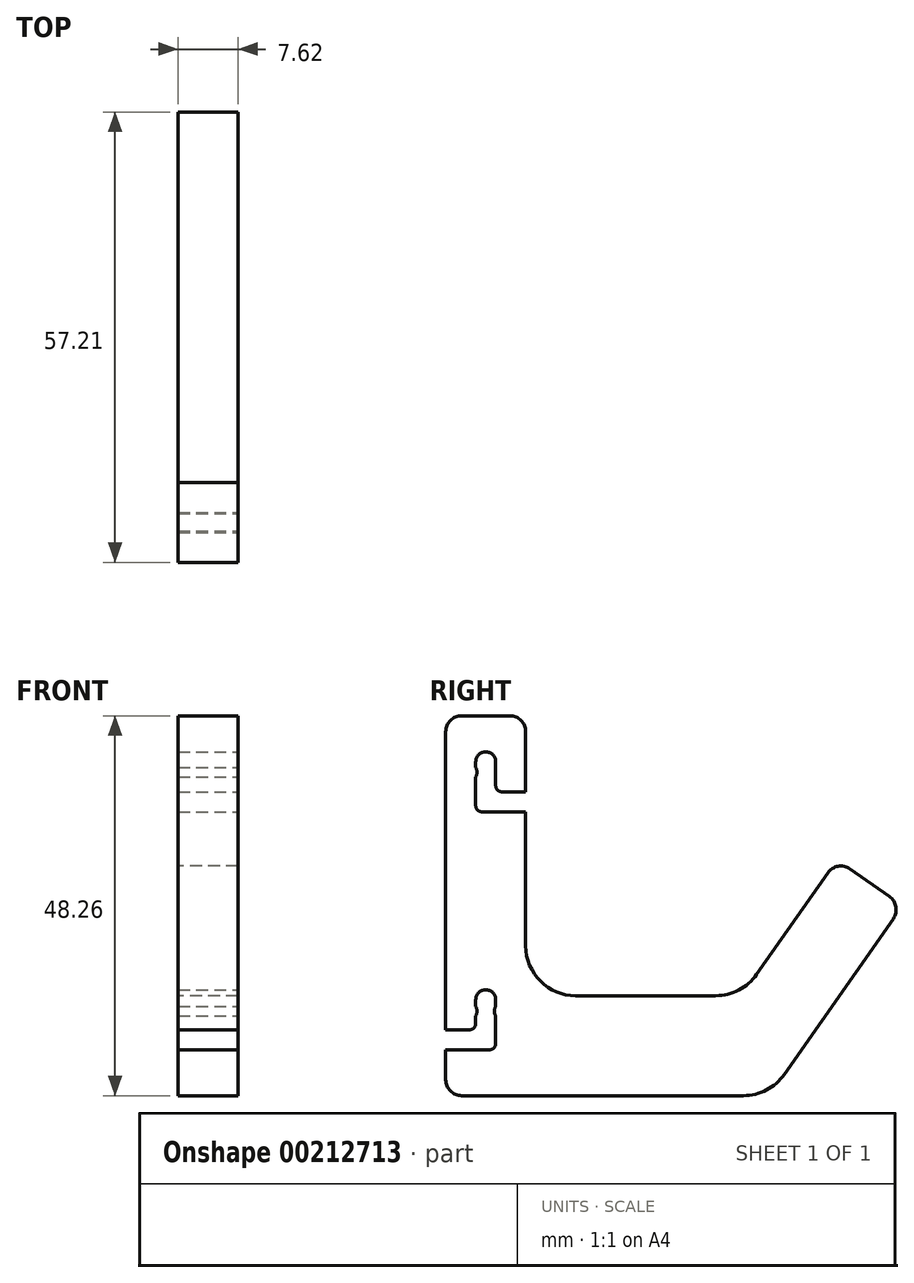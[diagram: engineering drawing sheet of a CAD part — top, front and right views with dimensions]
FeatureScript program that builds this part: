
annotation { "Feature Type Name" : "Feature", "Feature Type Description" : "" }
export const myFeature = defineFeature(function(context is Context, id is Id, definition is map)
    precondition{}
    {
        {
            var Q0;
            Q0=qCreatedBy(makeId("Right.planeOp"),FACE);
            var sketch = newSketch(context, id + "F0", { "sketchPlane" : qUnion([Q0])});
            skLineSegment(sketch, "E0", {"start": v(0, 0) * mm, "end": v(0, 43.18) * mm});
            skLineSegment(sketch, "E1", {"start": v(0, 43.18) * mm, "end": v(10.16, 43.18) * mm});
            skLineSegment(sketch, "E2", {"start": v(10.16, 43.18) * mm, "end": v(10.16, 13.97) * mm});
            skLineSegment(sketch, "E3", {"start": v(0, 0) * mm, "end": v(0, 0) * mm});
            skLineSegment(sketch, "E4", {"start": v(16.51, 7.62) * mm, "end": v(34.3, 7.62) * mm});
            skLineSegment(sketch, "E5", {"start": v(39.5, 10.33) * mm, "end": v(49.69, 24.9) * mm});
            skLineSegment(sketch, "E6", {"start": v(49.69, 24.9) * mm, "end": v(58.01, 19.06) * mm});
            skLineSegment(sketch, "E7", {"start": v(58.01, 19.06) * mm, "end": v(43, -2.37) * mm});
            skArc(sketch, "E8", {"start": v(34.3, 7.62) * mm, "mid": v(37.22, 8.34) * mm, "end": v(39.5, 10.33) * mm});
            skArc(sketch, "E9", {"start": v(10.16, 13.97) * mm, "mid": v(12.02, 9.48) * mm, "end": v(16.51, 7.62) * mm});
            skArc(sketch, "E10.filletArc", {"start": v(37.8, -5.08) * mm, "mid": v(40.73, -4.36) * mm, "end": v(43, -2.37) * mm});
            skLineSegment(sketch, "E11", {"start": v(0, 0) * mm, "end": v(0, -5.08) * mm});
            skLineSegment(sketch, "E12", {"start": v(0, -5.08) * mm, "end": v(37.8, -5.08) * mm});
            skSolve(sketch);
        }
        {
            var Q0;
            Q0=makeQuery(id+"F0.imprint","IMPRINT",FACE,{"disambiguationData":[TD([[makeQuery(id+"F0.imprint","IMPRINT",EDGE,{"derivedFrom":sQuery(id+"F0.wireOp",EDGE,"E0")}),-1.0]])]});
            extrude(context, id + "F1", {"entities" : qUnion([Q0]), "depth" : 7.62 * mm, "symmetric" : true});
        }
        {
            var Q0;
            Q0=makeQuery(id+"F1.opExtrude","SWEPT_EDGE",EDGE,{"disambiguationData":[OSD([sQuery(id+"F0.wireOp",EDGE,"E1"),sQuery(id+"F0.wireOp",EDGE,"E2")])]});
            var Q1;
            Q1=makeQuery(id+"F1.opExtrude","SWEPT_EDGE",EDGE,{"disambiguationData":[OSD([sQuery(id+"F0.wireOp",EDGE,"do6iOSd0-p59h-Iph2-EZYE-FqhHj6ALnol1"),sQuery(id+"F0.wireOp",EDGE,"T0NzOJQf-1ohU-N6pa-0O5Z-Gt8aX7xeZM4e")])]});
            var Q2;
            Q2=makeQuery(id+"F1.opExtrude","SWEPT_EDGE",EDGE,{"disambiguationData":[OSD([sQuery(id+"F0.wireOp",EDGE,"do6iOSd0-p59h-Iph2-EZYE-FqhHj6ALnol1"),sQuery(id+"F0.wireOp",EDGE,"WKioYHe8-msfK-nLwt-kgpN-sC7kTCiPyutY")])]});
            var Q3;
            Q3=makeQuery(id+"F1.opExtrude","SWEPT_EDGE",EDGE,{"disambiguationData":[OSD([sQuery(id+"F0.wireOp",EDGE,"do6iOSd0-p59h-Iph2-EZYE-FqhHj6ALnol1"),sQuery(id+"F0.wireOp",EDGE,"T0NzOJQf-1ohU-N6pa-0O5Z-Gt8aX7xeZM4e")])]});
            var Q4;
            Q4=makeQuery(id+"F1.opExtrude","SWEPT_EDGE",EDGE,{"disambiguationData":[OSD([sQuery(id+"F0.wireOp",EDGE,"do6iOSd0-p59h-Iph2-EZYE-FqhHj6ALnol1"),sQuery(id+"F0.wireOp",EDGE,"WKioYHe8-msfK-nLwt-kgpN-sC7kTCiPyutY")])]});
            var Q5;
            Q5=makeQuery(id+"F1.opExtrude","SWEPT_EDGE",EDGE,{"disambiguationData":[OSD([sQuery(id+"F0.wireOp",EDGE,"E1"),sQuery(id+"F0.wireOp",EDGE,"917d6a71-8020-47b3-91d0-356564592358.trimOffspring")])]});
            var Q6;
            Q6=makeQuery(id+"F1.opExtrude","SWEPT_EDGE",EDGE,{"disambiguationData":[OSD([sQuery(id+"F0.wireOp",EDGE,"E1"),sQuery(id+"F0.wireOp",EDGE,"E2")])]});
            var Q7;
            Q7=makeQuery(id+"F1.opExtrude","SWEPT_EDGE",EDGE,{"disambiguationData":[OSD([sQuery(id+"F0.wireOp",EDGE,"E1"),sQuery(id+"F0.wireOp",EDGE,"917d6a71-8020-47b3-91d0-356564592358.trimOffspring")])]});
            var Q8;
            Q8=makeQuery(id+"F1.opExtrude","SWEPT_EDGE",EDGE,{"disambiguationData":[OSD([sQuery(id+"F0.wireOp",EDGE,"E1"),sQuery(id+"F0.wireOp",EDGE,"917d6a71-8020-47b3-91d0-356564592358.trimOffspring")])]});
            var Q9;
            Q9=makeQuery(id+"F1.opExtrude","SWEPT_EDGE",EDGE,{"disambiguationData":[OSD([sQuery(id+"F0.wireOp",EDGE,"917d6a71-8020-47b3-91d0-356564592358.trimOffspring"),sQuery(id+"F0.wireOp",EDGE,"oMnLxIvI-c7EB-dOBx-Ktot-nHqWXF2Je9gS")])]});
            var Q10;
            Q10=makeQuery(id+"F1.opExtrude","SWEPT_EDGE",EDGE,{"disambiguationData":[OSD([sQuery(id+"F0.wireOp",EDGE,"E0"),sQuery(id+"F0.wireOp",EDGE,"H5s6PmsO-nB2p-iTXC-beMi-EFhrGGPzX9zd")])]});
            var Q11;
            Q11=makeQuery(id+"F1.opExtrude","SWEPT_EDGE",EDGE,{"disambiguationData":[OSD([sQuery(id+"F0.wireOp",EDGE,"E0"),sQuery(id+"F0.wireOp",EDGE,"H5s6PmsO-nB2p-iTXC-beMi-EFhrGGPzX9zd")])]});
            var Q12;
            Q12=makeQuery(id+"F1.opExtrude","SWEPT_EDGE",EDGE,{"disambiguationData":[OSD([sQuery(id+"F0.wireOp",EDGE,"E0"),sQuery(id+"F0.wireOp",EDGE,"H5s6PmsO-nB2p-iTXC-beMi-EFhrGGPzX9zd")])]});
            var Q13;
            Q13=makeQuery(id+"F1.opExtrude","SWEPT_EDGE",EDGE,{"disambiguationData":[OSD([sQuery(id+"F0.wireOp",EDGE,"E0"),sQuery(id+"F0.wireOp",EDGE,"H5s6PmsO-nB2p-iTXC-beMi-EFhrGGPzX9zd")])]});
            var Q14;
            Q14=makeQuery(id+"F1.opExtrude","SWEPT_EDGE",EDGE,{"disambiguationData":[OSD([sQuery(id+"F0.wireOp",EDGE,"tsVY66jG-GQxW-Nj7m-msUx-ij5FFVlZpnMZ"),sQuery(id+"F0.wireOp",EDGE,"p4fpiYAK-jGJt-w9eP-5vz1-EoqmOrb9To5q")])]});
            var Q15;
            Q15=makeQuery(id+"F1.opExtrude","SWEPT_EDGE",EDGE,{"disambiguationData":[OSD([sQuery(id+"F0.wireOp",EDGE,"tsVY66jG-GQxW-Nj7m-msUx-ij5FFVlZpnMZ"),sQuery(id+"F0.wireOp",EDGE,"pGC2duow-bWWV-YhgJ-DpL9-4p7fWgwL10ZT")])]});
            var Q16;
            Q16=makeQuery(id+"F1.opExtrude","SWEPT_EDGE",EDGE,{"disambiguationData":[OSD([sQuery(id+"F0.wireOp",EDGE,"tsVY66jG-GQxW-Nj7m-msUx-ij5FFVlZpnMZ"),sQuery(id+"F0.wireOp",EDGE,"pGC2duow-bWWV-YhgJ-DpL9-4p7fWgwL10ZT")])]});
            var Q17;
            Q17=makeQuery(id+"F1.opExtrude","SWEPT_EDGE",EDGE,{"disambiguationData":[OSD([sQuery(id+"F0.wireOp",EDGE,"tsVY66jG-GQxW-Nj7m-msUx-ij5FFVlZpnMZ"),sQuery(id+"F0.wireOp",EDGE,"p4fpiYAK-jGJt-w9eP-5vz1-EoqmOrb9To5q")])]});
            var Q18;
            Q18=makeQuery(id+"F1.opExtrude","SWEPT_EDGE",EDGE,{"disambiguationData":[OSD([sQuery(id+"F0.wireOp",EDGE,"tsVY66jG-GQxW-Nj7m-msUx-ij5FFVlZpnMZ"),sQuery(id+"F0.wireOp",EDGE,"pGC2duow-bWWV-YhgJ-DpL9-4p7fWgwL10ZT")])]});
            var Q19;
            Q19=makeQuery(id+"F1.opExtrude","SWEPT_EDGE",EDGE,{"disambiguationData":[OSD([sQuery(id+"F0.wireOp",EDGE,"l7jfHRW3-1uXe-nOm0-suk0-xWNmDAWcYurH"),sQuery(id+"F0.wireOp",EDGE,"E3")])]});
            var Q20;
            Q20=makeQuery(id+"F1.opExtrude","SWEPT_EDGE",EDGE,{"disambiguationData":[OSD([sQuery(id+"F0.wireOp",EDGE,"E5"),sQuery(id+"F0.wireOp",EDGE,"E6")])]});
            var Q21;
            Q21=makeQuery(id+"F1.opExtrude","SWEPT_EDGE",EDGE,{"disambiguationData":[OSD([sQuery(id+"F0.wireOp",EDGE,"E6"),sQuery(id+"F0.wireOp",EDGE,"E7")])]});
            var Q22;
            Q22=makeQuery(id+"F1.opExtrude","SWEPT_EDGE",EDGE,{"disambiguationData":[OSD([sQuery(id+"F0.wireOp",EDGE,"E11"),sQuery(id+"F0.wireOp",EDGE,"E12")])]});
            fillet(context, id + "F2", {"entities" : qUnion([Q0, Q1, Q2, Q3, Q4, Q5, Q6, Q7, Q8, Q9, Q10, Q11, Q12, Q13, Q14, Q15, Q16, Q17, Q18, Q19, Q20, Q21, Q22]), "radius" : 2.03 * mm, "tangentPropagation" : true, "allowEdgeOverflow" : false});
        }
        {
            var Q0;
            Q0=makeQuery(id+"F1.opExtrude","CAP_FACE",FACE,{"disambiguationData":[OSD([sQuery(id+"F0.wireOp",EDGE,"E0"),sQuery(id+"F0.wireOp",EDGE,"E1"),sQuery(id+"F0.wireOp",EDGE,"917d6a71-8020-47b3-91d0-356564592358.trimOffspring"),sQuery(id+"F0.wireOp",EDGE,"do6iOSd0-p59h-Iph2-EZYE-FqhHj6ALnol1"),sQuery(id+"F0.wireOp",EDGE,"E2"),sQuery(id+"F0.wireOp",EDGE,"oMnLxIvI-c7EB-dOBx-Ktot-nHqWXF2Je9gS"),sQuery(id+"F0.wireOp",EDGE,"H5s6PmsO-nB2p-iTXC-beMi-EFhrGGPzX9zd"),sQuery(id+"F0.wireOp",EDGE,"E55nDa4c-AnYE-asiw-xueP-FGOoVfwC6I5W"),sQuery(id+"F0.wireOp",EDGE,"tsVY66jG-GQxW-Nj7m-msUx-ij5FFVlZpnMZ"),sQuery(id+"F0.wireOp",EDGE,"WKioYHe8-msfK-nLwt-kgpN-sC7kTCiPyutY"),sQuery(id+"F0.wireOp",EDGE,"pGC2duow-bWWV-YhgJ-DpL9-4p7fWgwL10ZT"),sQuery(id+"F0.wireOp",EDGE,"l7jfHRW3-1uXe-nOm0-suk0-xWNmDAWcYurH"),sQuery(id+"F0.wireOp",EDGE,"p4fpiYAK-jGJt-w9eP-5vz1-EoqmOrb9To5q"),sQuery(id+"F0.wireOp",EDGE,"E3"),sQuery(id+"F0.wireOp",EDGE,"yA7TRvCN-UMRo-vrpZ-Ydxq-uWrTOSylFOQI"),sQuery(id+"F0.wireOp",EDGE,"T0NzOJQf-1ohU-N6pa-0O5Z-Gt8aX7xeZM4e"),sQuery(id+"F0.wireOp",EDGE,"pUJUahGI-wT5O-X5Pp-sLFv-ISeCsSa39cJM"),sQuery(id+"F0.wireOp",EDGE,"gnTElwEQ-xExs-yJdp-y54U-xUUldCR7EacK"),sQuery(id+"F0.wireOp",EDGE,"427NVwON-J4Eg-A1F7-4Q2u-34sglIcidLrh")])],"isStart":false});
            var sketch = newSketch(context, id + "F3", { "sketchPlane" : qUnion([Q0])});
            skLineSegment(sketch, "E13", {"start": v(5.08, 37.34) * mm, "end": v(5.08, 7.11) * mm, "construction": true});
            skArc(sketch, "E14", {"start": v(6.35, 37.34) * mm, "mid": v(5.08, 38.6) * mm, "end": v(3.81, 37.34) * mm});
            skLineSegment(sketch, "E15", {"start": v(3.81, 37.34) * mm, "end": v(3.81, 30.99) * mm});
            skLineSegment(sketch, "E16", {"start": v(3.81, 30.99) * mm, "end": v(10.16, 30.99) * mm});
            skLineSegment(sketch, "E17", {"start": v(10.16, 30.99) * mm, "end": v(10.16, 33.53) * mm});
            skLineSegment(sketch, "E18", {"start": v(10.16, 33.53) * mm, "end": v(6.35, 33.53) * mm});
            skLineSegment(sketch, "E19", {"start": v(6.35, 33.53) * mm, "end": v(6.35, 37.34) * mm});
            skLineSegment(sketch, "E20", {"start": v(5.08, 37.34) * mm, "end": v(5.08, 43.18) * mm, "construction": true});
            skArc(sketch, "E21", {"start": v(6.35, 7.11) * mm, "mid": v(5.08, 8.38) * mm, "end": v(3.81, 7.11) * mm});
            skLineSegment(sketch, "E22", {"start": v(3.81, 7.11) * mm, "end": v(3.81, 3.3) * mm});
            skLineSegment(sketch, "E23", {"start": v(3.81, 3.3) * mm, "end": v(0, 3.3) * mm});
            skLineSegment(sketch, "E24", {"start": v(0, 3.3) * mm, "end": v(0, 0.76) * mm});
            skLineSegment(sketch, "E25", {"start": v(0, 0.76) * mm, "end": v(6.35, 0.76) * mm});
            skLineSegment(sketch, "E26", {"start": v(6.35, 0.76) * mm, "end": v(6.35, 7.11) * mm});
            skSolve(sketch);
        }
        {
            var Q0;
            Q0=qSketchRegion(id+"F3",true);
            extrude(context, id + "F4", {"entities" : qUnion([Q0]), "operationType" : NewBodyOperationType.REMOVE, "endBound" : BoundingType.THROUGH_ALL, "oppositeDirection" : true, "depth" : 25.4 * mm});
        }
        {
            var Q0;
            Q0=makeQuery(id+"F4.boolean.opBoolean","COPY",EDGE,{"derivedFrom":makeQuery(id+"F4.opExtrude","SWEPT_EDGE",EDGE,{"disambiguationData":[OSD([sQuery(id+"F3.wireOp",EDGE,"E18"),sQuery(id+"F3.wireOp",EDGE,"E19")])]})});
            var Q1;
            Q1=makeQuery(id+"F4.boolean.opBoolean","COPY",EDGE,{"derivedFrom":makeQuery(id+"F4.opExtrude","SWEPT_EDGE",EDGE,{"disambiguationData":[OSD([sQuery(id+"F0.wireOp",EDGE,"E2"),sQuery(id+"F3.wireOp",EDGE,"E17"),sQuery(id+"F3.wireOp",EDGE,"E18")])]})});
            var Q2;
            Q2=makeQuery(id+"F4.boolean.opBoolean","COPY",EDGE,{"derivedFrom":makeQuery(id+"F4.opExtrude","SWEPT_EDGE",EDGE,{"disambiguationData":[OSD([sQuery(id+"F3.wireOp",EDGE,"E15"),sQuery(id+"F3.wireOp",EDGE,"E16")])]})});
            var Q3;
            Q3=makeQuery(id+"F4.boolean.opBoolean","COPY",EDGE,{"derivedFrom":makeQuery(id+"F4.opExtrude","SWEPT_EDGE",EDGE,{"disambiguationData":[OSD([sQuery(id+"F0.wireOp",EDGE,"E2"),sQuery(id+"F3.wireOp",EDGE,"E16"),sQuery(id+"F3.wireOp",EDGE,"E17")])]})});
            var Q4;
            Q4=makeQuery(id+"F4.boolean.opBoolean","COPY",EDGE,{"derivedFrom":makeQuery(id+"F4.opExtrude","SWEPT_EDGE",EDGE,{"disambiguationData":[OSD([sQuery(id+"F0.wireOp",EDGE,"E0"),sQuery(id+"F0.wireOp",EDGE,"E3"),sQuery(id+"F3.wireOp",EDGE,"E23"),sQuery(id+"F3.wireOp",EDGE,"E24")])]})});
            var Q5;
            Q5=makeQuery(id+"F4.boolean.opBoolean","COPY",EDGE,{"derivedFrom":makeQuery(id+"F4.opExtrude","SWEPT_EDGE",EDGE,{"disambiguationData":[OSD([sQuery(id+"F3.wireOp",EDGE,"E25"),sQuery(id+"F3.wireOp",EDGE,"E26")])]})});
            var Q6;
            Q6=makeQuery(id+"F4.boolean.opBoolean","COPY",EDGE,{"derivedFrom":makeQuery(id+"F4.opExtrude","SWEPT_EDGE",EDGE,{"disambiguationData":[OSD([sQuery(id+"F0.wireOp",EDGE,"E0"),sQuery(id+"F0.wireOp",EDGE,"E3"),sQuery(id+"F3.wireOp",EDGE,"E24"),sQuery(id+"F3.wireOp",EDGE,"E25")])]})});
            var Q7;
            Q7=makeQuery(id+"F4.boolean.opBoolean","COPY",EDGE,{"derivedFrom":makeQuery(id+"F4.opExtrude","SWEPT_EDGE",EDGE,{"disambiguationData":[OSD([sQuery(id+"F3.wireOp",EDGE,"E22"),sQuery(id+"F3.wireOp",EDGE,"E23")])]})});
            fillet(context, id + "F5", {"entities" : qUnion([Q0, Q1, Q2, Q3, Q4, Q5, Q6, Q7]), "radius" : 0.76 * mm, "tangentPropagation" : true, "allowEdgeOverflow" : false});
        }
        {
            var Q0;
            Q0=makeQuery(id+"F1.opExtrude","CAP_FACE",FACE,{"disambiguationData":[OSD([sQuery(id+"F0.wireOp",EDGE,"E0"),sQuery(id+"F0.wireOp",EDGE,"E1"),sQuery(id+"F0.wireOp",EDGE,"E2"),sQuery(id+"F0.wireOp",EDGE,"tsVY66jG-GQxW-Nj7m-msUx-ij5FFVlZpnMZ"),sQuery(id+"F0.wireOp",EDGE,"WKioYHe8-msfK-nLwt-kgpN-sC7kTCiPyutY"),sQuery(id+"F0.wireOp",EDGE,"pGC2duow-bWWV-YhgJ-DpL9-4p7fWgwL10ZT"),sQuery(id+"F0.wireOp",EDGE,"l7jfHRW3-1uXe-nOm0-suk0-xWNmDAWcYurH"),sQuery(id+"F0.wireOp",EDGE,"p4fpiYAK-jGJt-w9eP-5vz1-EoqmOrb9To5q"),sQuery(id+"F0.wireOp",EDGE,"E3")])],"isStart":false});
            var sketch = newSketch(context, id + "F6", { "sketchPlane" : qUnion([Q0])});
            skArc(sketch, "E27", {"start": v(3.81, 35.4) * mm, "mid": v(3.98, 36) * mm, "end": v(3.81, 36.6) * mm});
            skCircle(sketch, "E28", {"center": v(5.08, 37.34) * mm, "radius": 1.19 * mm, "construction": true});
            skLineSegment(sketch, "E29", {"start": v(5.08, 37.34) * mm, "end": v(5.08, 20.83) * mm, "construction": true});
            skLineSegment(sketch, "E30", {"start": v(3.81, 35.4) * mm, "end": v(6.35, 35.4) * mm, "construction": true});
            skLineSegment(sketch, "E31", {"start": v(3.81, 36.6) * mm, "end": v(6.35, 36.6) * mm, "construction": true});
            skArc(sketch, "E32.MirrorCS", {"start": v(6.35, 35.4) * mm, "mid": v(6.18, 36) * mm, "end": v(6.35, 36.6) * mm});
            skLineSegment(sketch, "E33", {"start": v(3.81, 36.6) * mm, "end": v(3.81, 35.4) * mm});
            skLineSegment(sketch, "E34.MirrorCS", {"start": v(6.35, 36.6) * mm, "end": v(6.35, 35.4) * mm});
            skLineSegment(sketch, "E35", {"start": v(5.08, 20.83) * mm, "end": v(0, 20.83) * mm, "construction": true});
            skCircle(sketch, "E36", {"center": v(5.08, 7.11) * mm, "radius": 1.19 * mm, "construction": true});
            skLineSegment(sketch, "E37", {"start": v(5.08, 20.83) * mm, "end": v(5.08, 4.32) * mm, "construction": true});
            skLineSegment(sketch, "E38.MirrorCS", {"start": v(3.81, 5.06) * mm, "end": v(3.81, 6.25) * mm});
            skArc(sketch, "E39.MirrorCS", {"start": v(3.81, 6.25) * mm, "mid": v(3.98, 5.65) * mm, "end": v(3.81, 5.06) * mm});
            skArc(sketch, "E40.MirrorCS", {"start": v(6.35, 6.25) * mm, "mid": v(6.18, 5.65) * mm, "end": v(6.35, 5.06) * mm});
            skLineSegment(sketch, "E41.MirrorCS", {"start": v(6.35, 5.06) * mm, "end": v(6.35, 6.25) * mm});
            skSolve(sketch);
        }
        {
            var Q0;
            Q0=makeQuery(id+"F6.imprint","IMPRINT",FACE,{"disambiguationData":[TD([[makeQuery(id+"F6.imprint","IMPRINT",EDGE,{"derivedFrom":sQuery(id+"F6.wireOp",EDGE,"E32.MirrorCS")}),-1.0]])]});
            var Q1;
            Q1=makeQuery(id+"F6.imprint","IMPRINT",FACE,{"disambiguationData":[TD([[makeQuery(id+"F6.imprint","IMPRINT",EDGE,{"derivedFrom":sQuery(id+"F6.wireOp",EDGE,"E27")}),1.0]])]});
            var Q2;
            Q2=makeQuery(id+"F6.imprint","IMPRINT",FACE,{"disambiguationData":[TD([[makeQuery(id+"F6.imprint","IMPRINT",EDGE,{"derivedFrom":sQuery(id+"F6.wireOp",EDGE,"E38.MirrorCS")}),1.0]])]});
            var Q3;
            Q3=makeQuery(id+"F6.imprint","IMPRINT",FACE,{"disambiguationData":[TD([[makeQuery(id+"F6.imprint","IMPRINT",EDGE,{"derivedFrom":sQuery(id+"F6.wireOp",EDGE,"E40.MirrorCS")}),1.0]])]});
            var Q4;
            Q4=makeQuery(id+"F1.opExtrude","CAP_FACE",FACE,{"disambiguationData":[OSD([sQuery(id+"F0.wireOp",EDGE,"E0"),sQuery(id+"F0.wireOp",EDGE,"E1"),sQuery(id+"F0.wireOp",EDGE,"E2"),sQuery(id+"F0.wireOp",EDGE,"tsVY66jG-GQxW-Nj7m-msUx-ij5FFVlZpnMZ"),sQuery(id+"F0.wireOp",EDGE,"WKioYHe8-msfK-nLwt-kgpN-sC7kTCiPyutY"),sQuery(id+"F0.wireOp",EDGE,"pGC2duow-bWWV-YhgJ-DpL9-4p7fWgwL10ZT"),sQuery(id+"F0.wireOp",EDGE,"l7jfHRW3-1uXe-nOm0-suk0-xWNmDAWcYurH"),sQuery(id+"F0.wireOp",EDGE,"p4fpiYAK-jGJt-w9eP-5vz1-EoqmOrb9To5q"),sQuery(id+"F0.wireOp",EDGE,"E3")])],"isStart":true});
            extrude(context, id + "F7", {"entities" : qUnion([Q0, Q1, Q2, Q3]), "operationType" : NewBodyOperationType.ADD, "endBound" : BoundingType.UP_TO_SURFACE, "oppositeDirection" : true, "endBoundEntityFace" : qUnion([Q4]), "depth" : 25.4 * mm});
        }
    });
